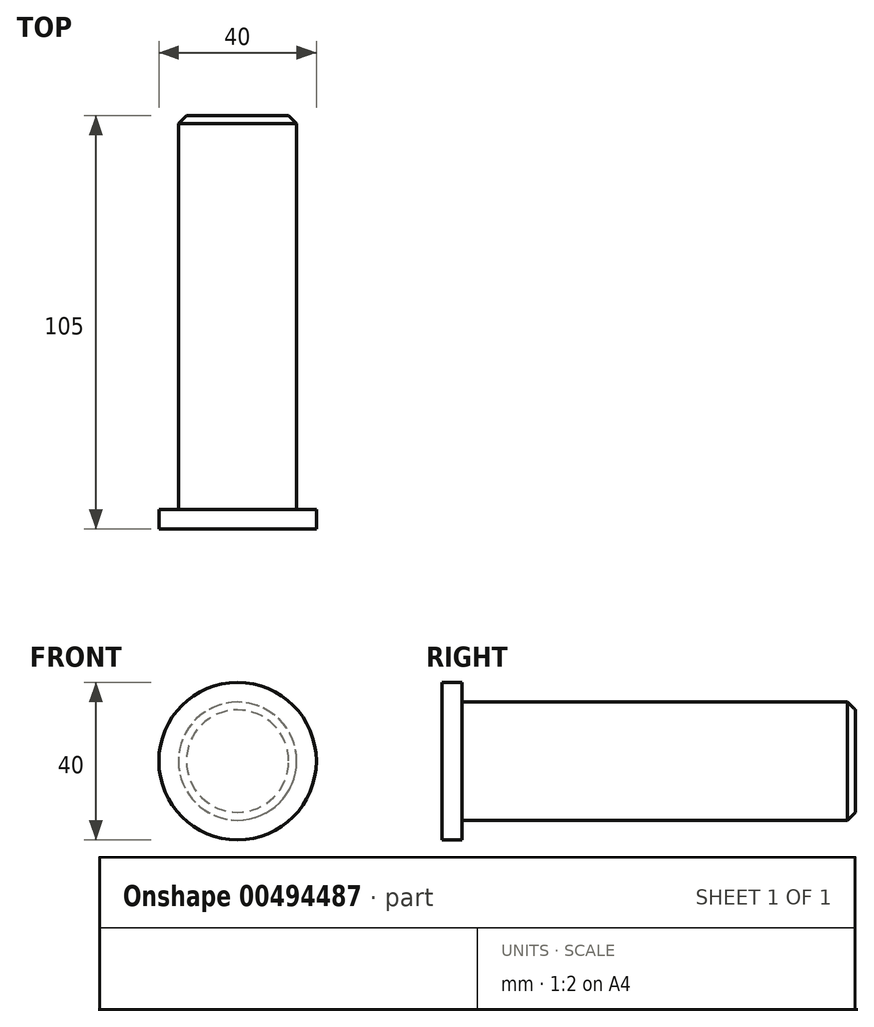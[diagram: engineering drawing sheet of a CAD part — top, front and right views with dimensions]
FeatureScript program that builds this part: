
annotation { "Feature Type Name" : "Feature", "Feature Type Description" : "" }
export const myFeature = defineFeature(function(context is Context, id is Id, definition is map)
    precondition{}
    {
        {
            var Q0;
            Q0=qCreatedBy(makeId("Right.planeOp"),FACE);
            var sketch = newSketch(context, id + "F0", { "sketchPlane" : qUnion([Q0])});
            skLineSegment(sketch, "E0", {"start": v(-5, 0) * mm, "end": v(-5, 20) * mm});
            skLineSegment(sketch, "E1", {"start": v(-5, 20) * mm, "end": v(0, 20) * mm});
            skLineSegment(sketch, "E2", {"start": v(0, 20) * mm, "end": v(0, 15) * mm});
            skLineSegment(sketch, "E3", {"start": v(0, 15) * mm, "end": v(100, 15) * mm});
            skLineSegment(sketch, "E4", {"start": v(100, 15) * mm, "end": v(100, 0) * mm});
            skLineSegment(sketch, "E5", {"start": v(-29.58, 0) * mm, "end": v(86.6, 0) * mm, "construction": true});
            skLineSegment(sketch, "E6", {"start": v(-5, 0) * mm, "end": v(100, 0) * mm});
            skSolve(sketch);
        }
        {
            var Q0;
            Q0=makeQuery(id+"F0.imprint","IMPRINT",FACE,{"disambiguationData":[TD([[makeQuery(id+"F0.imprint","IMPRINT",EDGE,{"derivedFrom":sQuery(id+"F0.wireOp",EDGE,"E0")}),-1.0]])]});
            var Q1;
            Q1=sQuery(id+"F0.wireOp",EDGE,"E5");
            revolve(context, id + "F1", {"entities" : qUnion([Q0]), "axis" : qUnion([Q1]), "revolveType" : RevolveType.FULL});
        }
        {
            var Q0;
            Q0=makeQuery(id+"F1.opRevolve","SWEPT_EDGE",EDGE,{"disambiguationData":[OSD([sQuery(id+"F0.wireOp",EDGE,"E3"),sQuery(id+"F0.wireOp",EDGE,"E4")])]});
            chamfer(context, id + "F2", {"entities" : qUnion([Q0]), "width" : 2 * mm, "tangentPropagation" : true});
        }
    });
